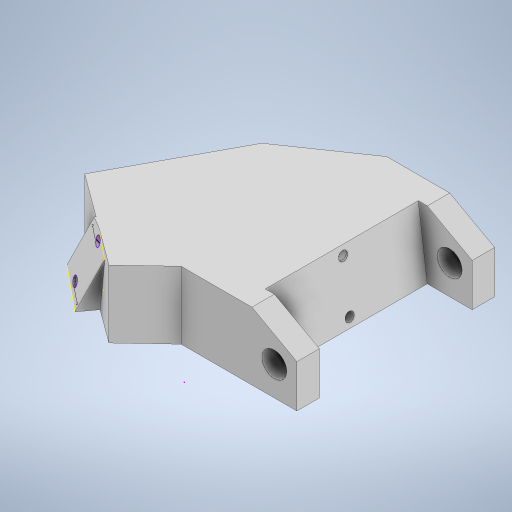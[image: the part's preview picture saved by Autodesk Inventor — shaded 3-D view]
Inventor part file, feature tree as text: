
AUTODESK INVENTOR PART (.ipt)
format: ipt  version: 2024 (Build 280153000, 153)  size: 911,360 bytes
history: native  units: mm
features: sketch x64, extrude x50, move_body x9, plane x6, split x6, boolean_combine x4, chamfer x3, loft x2, delete_face x1
ambient origin geometry x8: Origin, YZ Plane, XZ Plane, XY Plane, X Axis, Y Axis, Z Axis, Center Point
bodies: Solid1 (feature_tree), Solid2 (feature_tree), Solid3 (feature_tree), Solid4 (feature_tree), Solid5 (feature_tree), Solid6 (feature_tree), Solid7 (feature_tree), Solid8 (feature_tree), Solid9 (feature_tree), Solid10 (feature_tree), Solid11 (feature_tree), Solid12 (feature_tree), Solid13 (feature_tree)
feature tree (145):
  extrude  "Extrusion1"  Depth=16.0mm
  sketch  "Sketch2"  dims[d2=15.0mm d3=0.0mm d4=10.0mm]
  extrude  "Extrusion2"  Depth=10.0mm
  chamfer  "Chamfer1"  Distance=21.25mm
  extrude  "Extrusion3"  Depth=10.0mm TaperAngle=0.0deg
  extrude  "Extrusion4"  Depth=11.5mm TaperAngle=0.0deg
  extrude  "Extrusion5"  Depth=1.0mm TaperAngle=0.0deg
  chamfer  "Chamfer2"  Distance=6.0mm Angle=45.0deg
  sketch  "Sketch6"  dims[d14=7.0mm d15=11.5mm d16=0.0mm]
  extrude  "Extrusion6"  Depth=9.0mm
  extrude  "Extrusion7"  Depth=45.25mm TaperAngle=0.0deg
  chamfer  "Chamfer3"  Distance=11.5mm Angle=45.0deg
  sketch  "Sketch9"  dims[d26=3.3mm d27=45.25mm d28=0.0mm d29=11.5mm d30=5.5mm d31=45.0deg]
  extrude  "Extrusion8"  Depth=65.75mm TaperAngle=0.0deg
  extrude  "Extrusion9"  Depth=9.0mm TaperAngle=0.0deg
  extrude  "Extrusion10"  Depth=13.0mm TaperAngle=0.0deg
  sketch  "Sketch13"  dims[d43=24.0mm d44=21.0mm d45=0.0mm]
  extrude  "Extrusion11"  Depth=21.0mm TaperAngle=0.0deg
  extrude  "Extrusion12"  TaperAngle=0.0deg  [1 undecoded]
  extrude  "Extrusion13"  Depth=1.0mm
  plane  "Work Plane1"
  split  "Split1"
  move_body  "Move Body1"
  extrude  "Extrusion14"  Depth=1.0mm TaperAngle=0.0deg
  delete_face  "Delete Face1"
  extrude  "Extrusion17"  Depth=1.0mm
  extrude  "Extrusion18"  Depth=1.2mm TaperAngle=0.0deg
  extrude  "Extrusion19"  [1 undecoded]
  extrude  "Extrusion20"  Depth=1.75mm
  plane  "Work Plane2"
  split  "Split2"
  move_body  "Move Body2"
  boolean_combine  "Combine1"
  plane  "Work Plane3"
  split  "Split3"
  move_body  "Move Body3"
  boolean_combine  "Combine2"
  split  "Split4"
  split  "Split5"
  move_body  "Move Body4"
  move_body  "Move Body5"
  extrude  "Extrusion22"  Depth=20.0mm TaperAngle=0.0deg
  extrude  "Extrusion23"  Depth=12.0mm
  move_body  "Move Body6"
  move_body  "Move Body7"
  boolean_combine  "Combine3"
  extrude  "Extrusion24"  Depth=12.0mm TaperAngle=0.0deg
  plane  "Work Plane5"
  sketch  "Sketch32"  dims[d110=8.0mm d111=0.0mm d112=5.5mm]
  plane  "Work Plane6"
  extrude  "Extrusion27"  Depth=8.0mm TaperAngle=0.0deg
  plane  "Work Plane4"
  extrude  "Extrusion28"  Depth=123.0mm TaperAngle=0.0deg
  sketch  "Sketch35"  dims[d121=2.0mm d122=0.0mm d123=8.0mm d124=0.0mm]
  extrude  "Extrusion29"  Depth=82.0mm TaperAngle=0.0deg
  extrude  "Extrusion30"  Depth=5.5mm
  extrude  "Extrusion31"  Depth=40.0mm TaperAngle=0.0deg
  sketch  "Sketch38"  dims[d131=15.0mm d132=0.0mm d133=15.0mm d134=0.0mm]
  extrude  "Extrusion32"  Depth=2.0mm TaperAngle=0.0deg
  extrude  "Extrusion33"  Depth=8.0mm TaperAngle=0.0deg
  extrude  "Extrusion34"  Depth=25.394541mm
  extrude  "Extrusion35"  Depth=15.0mm TaperAngle=0.0deg
  extrude  "Extrusion36"  Depth=15.0mm TaperAngle=0.0deg
  extrude  "Extrusion37"  Depth=15.0mm TaperAngle=0.0deg
  extrude  "Extrusion38"  Depth=15.0mm TaperAngle=0.0deg
  extrude  "Extrusion39"  Depth=6.75mm TaperAngle=0.0deg
  extrude  "Extrusion40"  Depth=10.0mm
  extrude  "Extrusion41"  Depth=2.0mm TaperAngle=0.0deg
  extrude  "Extrusion42"  Depth=9.0mm
  extrude  "Extrusion43"  Depth=20.5mm TaperAngle=0.0deg
  extrude  "Extrusion44"  Depth=22.0mm TaperAngle=0.0deg
  split  "Split6"
  move_body  "Move Body8"
  extrude  "Extrusion45"  Depth=10.0mm
  move_body  "Move Body9"
  boolean_combine  "Combine4"
  extrude  "Extrusion46"  Depth=13.706mm
  extrude  "Extrusion47"  Depth=1.95mm
  sketch  "Sketch56"  dims[d224=0.0mm d225=90.0deg d226=0.0mm d227=90.0deg]
  extrude  "Extrusion48"  Depth=4.0mm TaperAngle=0.0deg
  extrude  "Extrusion49"  Depth=3.25mm TaperAngle=0.0deg
  extrude  "Extrusion50"  TaperAngle=90.0deg  [1 undecoded]
  extrude  "Extrusion51"  Depth=2.0mm
  extrude  "Extrusion52"  TaperAngle=0.0deg  [1 undecoded]
  sketch  "Sketch67"  dims[d245=34.0mm d246=0.0mm]
  extrude  "Extrusion53"  Depth=2.0mm
  loft  "Loft3"
  loft  "Loft4"
  sketch  "Sketch73"  dims[d241=0.872665mm]
  sketch  "Sketch74"
  extrude  "Extrusion55"  Depth=2.0mm
  extrude  "Extrusion56"  Depth=2.0mm
  sketch  "Sketch1"  dims[d0=36.0mm d1=16.0mm]
  sketch  "Sketch3"  dims[d5=10.0mm]
  sketch  "Sketch4"  dims[d6=3.3mm d7=21.25mm d8=0.0mm]
  sketch  "Sketch5"  dims[d9=10.0mm d10=5.5mm d11=45.0deg d12=10.0mm d13=0.0mm]
  sketch  "Sketch7"  dims[d17=3.3mm d18=1.0mm d19=0.0mm d20=6.0mm d21=11.5mm d22=45.0deg]
  sketch  "Sketch8"  dims[d23=15.0mm d24=0.0mm d25=9.0mm]
  sketch  "Sketch10"  dims[d32=2.0mm d33=65.75mm d34=0.0mm]
  sketch  "Sketch11"  dims[d35=0.5mm d36=0.0mm d37=9.0mm d38=0.0mm]
  sketch  "Sketch12"  dims[d39=0.5mm d40=0.0mm d41=13.0mm d42=0.0mm]
  sketch  "Sketch14"  dims[d46=12.25mm d47=-12.0mm d48=0.0mm d49=0.0mm]
  sketch  "Sketch15"  dims[d50=10.0mm d51=0.0mm d61=1.0mm]
  sketch  "Sketch16"  dims[d62=1.0mm d63=1.5mm d64=0.0mm]
  sketch  "Sketch17"  dims[d65=1.0mm d66=1.0mm]
  sketch  "Sketch20"  dims[d67=5.5mm d68=0.0mm d69=1.2mm d70=0.0mm]
  sketch  "Sketch21"  dims[d71=2.2mm d72=0.0mm d73=-5.5mm]
  sketch  "Sketch22"  dims[d74=-3.0mm d75=0.0mm d76=0.0mm d79=1.75mm]
  sketch  "Sketch23"  dims[d80=3.0mm d81=0.0mm d82=0.0mm d83=0.0mm d84=0.0mm d85=20.0mm]
  sketch  "Sketch25"  dims[d86=0.0mm d87=0.0mm d88=-20.0mm d89=12.0mm]
  sketch  "Sketch26"  dims[d90=12.0mm d91=0.0mm d92=12.0mm d93=0.0mm]
  sketch  "Sketch27"  dims[d94=0.0mm d95=0.0mm d96=-8.0mm d97=0.0mm d98=0.0mm d99=8.0mm]
  sketch  "Sketch28"  dims[d100=4.5mm d101=123.0mm d102=0.0mm]
  sketch  "Sketch29"  dims[d107=5.1mm d108=82.0mm d109=0.0mm]
  sketch  "Sketch33"  dims[d113=40.0mm d114=0.0mm d115=40.0mm d116=0.0mm]
  sketch  "Sketch34"  dims[d117=40.0mm d118=0.0mm d119=2.0mm d120=0.0mm]
  sketch  "Sketch36"  dims[d125=20.0mm d126=25.394541mm]
  sketch  "Sketch37"  dims[d127=15.0mm d128=0.0mm d129=15.0mm d130=0.0mm]
  sketch  "Sketch39"  dims[d135=15.0mm d136=0.0mm d137=15.0mm d138=0.0mm]
  sketch  "Sketch40"  dims[d139=6.3338mm d140=15.0mm d141=0.0mm]
  sketch  "Sketch41"  dims[d142=15.0mm d143=0.0mm d144=6.75mm d145=0.0mm]
  sketch  "Sketch42"  dims[d146=30.0mm d147=0.0mm d148=10.0mm]
  sketch  "Sketch43"  dims[d149=-5.0mm d150=0.0mm d151=0.0mm d152=2.0mm d153=0.0mm]
  sketch  "Sketch44"  dims[d154=3.0mm d155=0.0mm d156=0.0mm d157=9.0mm]
  sketch  "Sketch45"  dims[d158=5.0mm d159=0.0mm d160=20.5mm d161=0.0mm]
  sketch  "Sketch46"  dims[d166=20.5mm d167=0.0mm d174=22.0mm d175=0.0mm]
  sketch  "Sketch47"  dims[d189=10.0mm d190=0.0mm d191=9.0mm]
  sketch  "Sketch48"  dims[d192=27.925268mm d193=13.706mm]
  sketch  "Sketch49"  dims[d194=2.0mm d195=1.95mm]
  sketch  "Sketch50"  dims[d197=2.0mm d198=4.0mm d199=0.0mm]
  sketch  "Sketch51"  dims[d200=11.25mm d201=0.0mm d202=3.25mm d203=0.0mm]
  sketch  "Sketch52"  dims[d204=2.0mm d205=90.0deg]
  sketch  "Sketch53"  dims[d207=2.0mm d212=2.0mm]
  sketch  "Sketch54"  dims[d214=0.0mm d215=90.0deg d216=0.0mm d217=90.0deg]
  sketch  "Sketch55"  dims[d220=2.0mm d223=2.0mm]
  sketch  "Sketch59"  dims[d231=2.0mm d232=2.0mm]
  sketch  "Sketch64"  dims[d233=34.0mm d238=2.0mm]
  sketch  "Sketch65"  dims[d239=2.0mm d242=2.0mm]
  sketch  "Sketch66"  dims[d243=34.0mm d244=0.0mm]
  sketch  "Sketch68"  dims[d52=0.5mm]
  sketch  "Sketch69"  dims[d53=0.872665mm]
  sketch  "Sketch70"  dims[d103=0.5mm]
  sketch  "Sketch71"  dims[d104=0.872665mm]
  sketch  "Sketch72"  dims[d240=0.5mm]
  sketch  "Sketch75"
note: 4 required parameter values undecoded (feature->parameter linkage not recoverable at this tier; creation-order binding heuristic only, values carry confidence <= 0.55)
